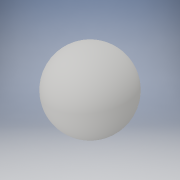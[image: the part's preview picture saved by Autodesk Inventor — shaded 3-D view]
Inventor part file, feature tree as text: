
AUTODESK INVENTOR PART (.ipt)
format: ipt  version: 2018 (Build 220112000, 112)  size: 116,736 bytes
history: native  units: in
note: dims shown in document units (in); Inventor stores cm internally (conversion verified against a paired STEP export)
features: revolve x1, sketch x1
ambient origin geometry x8: Origin, YZ Plane, XZ Plane, XY Plane, X Axis, Y Axis, Z Axis, Center Point
bodies: Solid1 (feature_tree)
feature tree (2):
  revolve  "Revolution1"  Angle=90.0deg
  sketch  "Sketch1"  dims[d0=0.625in d1=90.0deg]
